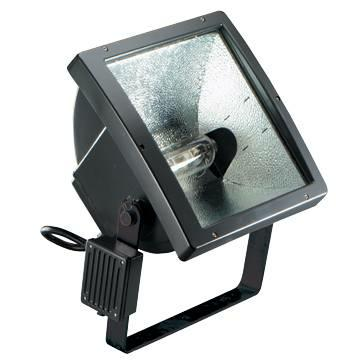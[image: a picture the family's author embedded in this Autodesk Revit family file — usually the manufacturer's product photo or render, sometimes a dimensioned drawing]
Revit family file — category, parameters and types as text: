
# Revit family: Lighting-Proiezione-GEWISS-COLOSSEUM-PROIETTORI_OTTICA_SIMMETRICA
name_source: partatom
category: Apparecchi per illuminazione
units: mm (PartAtom-declared; Revit-internal decimal feet)

## family parameters
Condiviso = No
Host = Superficie
Numero OmniClass = 23.80.70.11.14
Punto di calcolo locali = Sì
Quota connettore circolare = Usa diametro
Sorgente d'illuminazione = No
Taglio con vuoti quando caricato = No
Tipo di parte = Normale
Titolo OmniClass = General Luminaries, Directional

## types (9) — shared parameters
Applicazione = Esterno
Carico apparente = 1000 VA
Catalogo = LIGHTING
Catalogo Serie = COLOSSEUM
Certificazione DIN 18032-3 = Conforme
Classe isolamento = I
Classificazione carico = Illuminazione
Codice Electrocod = 2433
Colore = Grigio grafite
Distanza minima dall'oggetto illuminato = 3M
Grado di protezione = IP66
IDF = 337b4e20-7dcf-4b5c-8cd1-a09b02e429b6
IDT = e3fb4f7b-269b-4903-8aa9-695488925831
Immagine tipo = GW84646.jpg
Inquinamento luminoso = 0 cd/Klm
L_interna staffa = 515 mm  [stored 1.68963 ft]
Lampada = MN
Manopola di rotazione = <Per categoria>
Materiale = Alluminio
Numero di poli = 2
Produttore = GEWISS S.p.A.
Prospetto di default = 1219 mm
Resistenza agli urti = IK09
SEO = Proiettore
Scheda Tecnica = https://www.gewiss.com
Spessore staffa = 40 mm  [stored 0.131234 ft]
Staffa = <Per categoria>
Superficie laterale esposta al vento = 0,083M2
Superficie massima esposta al vento = 0,25M2
URL = https://www.gewiss.com
Versione file RFA = 20.11
Voltaggio = 230 V

## per-type parameters (varying)
| type | Attacco lampada | Codice EAN | Corrente lampada | Corrente lampada: | Descrizione | Lampada: | Modello | Ottica | Peso (kg) | Peso (kg): | Potenza lampada |
| GW84648 - COLOSSEUM SIM. DIF. 1000W MT 1kV E40 | E40 | 8011564073432 | 8,25A | 8,25A | COLOSSEUM OTTICA SIMMETRICA DIFFONDENTE 1000W MT 1kV E40 | MT* | GW84648 | Simmetrica diffondente - ULOR: 0% | 15,7 | 15,7 | 1000W |
| GW84749 - COLOSSEUM SIM. CON. 1000W MN X528/CAVO | X528/Cavo | 8011564222120 | 9,5A | 9,5A | COLOSSEUM OTTICA SIMMETRICA CONCENTRANTE 1000W MN X528/CAVO | MN | GW84749 | Simmetrica concentrante - ULOR: 0% | 16,4 | 16,4 | 1000W |
| GW84646 - COLOSSEUM SIM. DIF. 600W ST E40 | E40 | 8011564073418 | 6,2A | 6,2A | COLOSSEUM OTTICA SIMMETRICA DIFFONDENTE 600W ST E40 | ST | GW84646 | Simmetrica diffondente - ULOR: 0% | 16 | 16 | 600W |
| GW84748 - COLOSSEUM SIM. CON. 1000W MT 1kV E40 | E40 | 8011564099937 | 8,25A | 8,25A | COLOSSEUM OTTICA SIMMETRICA CONCENTRANTE 1000W MT 1kV E40 | MT* | GW84748 | Simmetrica concentrante - ULOR: 0% | 15,7 | 15,7 | 1000W |
| GW84647 - COLOSSEUM SIM. DIF. 1000W MT/ST E40 | E40 | 8011564073425 | 9,5-10,3A | 9,5-10,3A | COLOSSEUM OTTICA SIMMETRICA DIFFONDENTE 1000W MT/ST E40 | MT/ST | GW84647 | Simmetrica diffondente - ULOR: 0% | 16 | 16 | 1000W |
| GW84747 - COLOSSEUM SIM. CON. 1000W MT/ST E40 | E40 | 8011564099920 | 9,5-10,3A | 9,5-10,3A | COLOSSEUM OTTICA SIMMETRICA CONCENTRANTE 1000W MT/ST E40 | MT/ST | GW84747 | Simmetrica concentrante - ULOR: 0% | 16 | 16 | 1000W |
| GW84644 - COLOSSEUM SIM. DIF. 2000W MN X528/CAVO | X528/Cavo | 8011564065666 | 10,3A | 10,3A | COLOSSEUM OTTICA SIMMETRICA DIFFONDENTE 2000W MN X528/CAVO | MN | GW84644 | Simmetrica diffondente - ULOR: 0% | 16,4 | 16,4 | 2000W |
| GW84649 - COLOSSEUM SIM. DIF. 1000W MN X528/CAVO | X528/Cavo | 8011564222113 | 9,5A | 9,5A | COLOSSEUM OTTICA SIMMETRICA DIFFONDENTE 1000W MN X528/CAVO | MN | GW84649 | Simmetrica diffondente - ULOR: 0% | 16,4 | 16,4 | 1000W |
| GW84744 - COLOSSEUM SIM. CON. 2000W MN X528/CAVO | X528/Cavo | 8011564099944 | 10,3A | 10,3A | COLOSSEUM OTTICA SIMMETRICA CONCENTRANTE 2000W MN X528/CAVO | MN | GW84744 | Simmetrica concentrante - ULOR: 0% | 16,4 | 16,4 | 2000W |

note: [stored X ft] marks values corroborated as IEEE doubles in the binary element streams (Revit-internal decimal feet)
